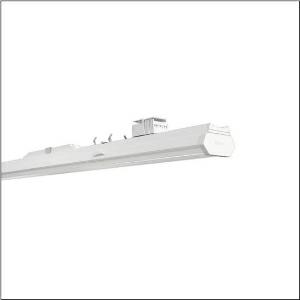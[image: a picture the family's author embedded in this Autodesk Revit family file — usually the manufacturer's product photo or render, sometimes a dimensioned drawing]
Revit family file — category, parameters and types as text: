
# Revit family: licross_r__21_protected_ho_52tp12dn4dxm_cc4f
name_source: partatom
category: Lighting Fixtures
units: mm (PartAtom-declared; Revit-internal decimal feet)

## family parameters
Cut with Voids When Loaded = No
Host = Face
Light Source = No
Part Type = Normal
Room Calculation Point = No
Round Connector Dimension = Use Diameter
Shared = No

## types (1)
- --- (1 x LED, 13000 lm, 74.3 W, 4000K)
    Apparent Load = 74 VA
    CIE Flux Codes = 70 91 97 98 100
    Color Rendering = 80
    Color Temperature = 4000K
    Default Elevation = 1800 mm
    Description = Licross® 21 Protected HO, luminaire insert, of sheet steel, galvanised, coil coated, white, length: 1.500mm, width: 90mm, height: 103mm, LED rated luminous flux: 13.000lm, light colour: 840, control gear: DALI 2, with plug, 5-pole, with phase selection, mains connection: 220..240V, AC, 50/60Hz, rated input power: 74W, halogen-free wiring, primary light control with lens, of plastic, primary optical cover: cover, of PMMA, light emission: direct distribution, primary light characteristic: symmetric, protection rating (complete): IP64, insulation class (complete): insulation class I (protective earthing), certification: CE, ENEC, VDE, UKCA, protection symbol: D if used in an environment with conductive dust loads with corresponding accessories, impact resistance: IK06, permissible ambient temperature for indoor applications: -25..+40°C, corresponds to IFS (International Featured Standards) requirements for safety and quality in the food industry, reducing of maximum allowable ambient temperature of 5°C with ceiling mounting, LABS conformity tested according to VDMA 24364:2018-05, packaging unit: 1 piece
    Height = 92 mm
    Lamp = 1 x LED
    Lamp Light Flux = 13000 lm
    Lamp Power = 74.3 W
    Lamp count = 1
    Length = 1500 mm
    Luminous efficacy = 175 lm/W
    Manufacturer = Siteco
    ModVariant = No
    Model = 52TP12DN4DXM
    Mounting Place = Ceiling
    Mounting Type = Pendant
    Number of Poles = 1
    OnlyDefault = Yes
    Power Factor = 1
    Product Name = Licross® 21 Protected HO
    Product group = luminaire insert
    ProductGroupID = 902
    Protection Class = Protection class I
    Protection Degree = IP 64
    RLX_Detail_Level = 1
    RLX_Emergency_Light_Flux = 0 lm
    RLX_Emergency_Type = 0
    RLX_Emergency_Type_DB = No
    RlxData = <blob elided: 24441 chars, md5=b1f3dc46>
    Socket = socket
    Standby Power = 0 W
    System Light Flux = 13000 lm
    System Power = 74 W
    Type Comments = factory setting: luminous flux: 100 % | dim-lin: 254 | 424 mA
    Type Image = l_1256148.jpg
    URL = http://relux.com
    VarID = @adj_128804
    Voltage = 0 V
    Weight = 0.00 kg
    Width = 88 mm

## geometry (parser evidence)
native form markers: Blend x4, Sweep x10
no freeform markers — native parametric forms only
